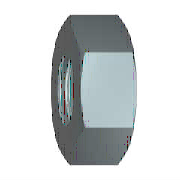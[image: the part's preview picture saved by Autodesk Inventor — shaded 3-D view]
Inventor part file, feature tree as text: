
AUTODESK INVENTOR PART (.ipt)
format: ipt  version: 2015 (Build 190159000, 159)  size: 165,376 bytes
history: native  units: mm (DEFAULTED — no unit token found)
features: sketch x3, other x2, extrude x1, hole x1, plane x1
ambient origin geometry x7: Origin, YZ Plane, XZ Plane, X Axis, Y Axis, Z Axis, Center Point
bodies: Body1 (feature_tree)
feature tree (8):
  extrude  "Bryła"  Depth=20.78461mm
  other  "Faza1"
  hole  "Gwint"  [1 undecoded]
  other  "Work Axis1"
  plane  "Work Plane1"
  sketch  "Szkic1"
  sketch  "Szkic2"
  sketch  "Szkic3"
note: 1 required parameter value undecoded (feature->parameter linkage not recoverable at this tier; creation-order binding heuristic only, values carry confidence <= 0.55)
